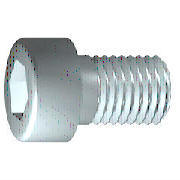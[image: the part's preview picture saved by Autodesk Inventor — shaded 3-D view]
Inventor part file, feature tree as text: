
AUTODESK INVENTOR PART (.ipt)
format: ipt  version: 2023.3 (Build 273359000, 359)  size: 196,096 bytes
history: native  units: mm (DEFAULTED — no unit token found)
features: sketch x2, other x1, extrude x1, plane x1, fillet x1
ambient origin geometry x7: Origin, YZ Plane, XY Plane, X Axis, Y Axis, Z Axis, Center Point
bodies: Solid1 (feature_tree)
feature tree (6):
  other  "Körper"
  extrude  "Loch"  Depth=2.0mm
  plane  "Work Plane1"
  fillet  "Fillet2"  Radius=2.0mm
  sketch  "Skizze1"  dims[d1=3.0mm d2=0.24548mm d3=2.0mm]
  sketch  "Skizze2"  dims[d4=1.0mm d5=60.0deg d6=2.0mm d7=2.0mm d8=1.732051mm d9=3.8mm d10=90.0deg d11=10.0mm d12=0.0mm d13=3.0mm d14=0.0mm d15=0.24538mm d16=0.24538mm d17=0.2mm d19=0.0mm d26=4.0mm d27=45.0deg d28=0.0mm d29=0.0mm d30=0.1mm]
